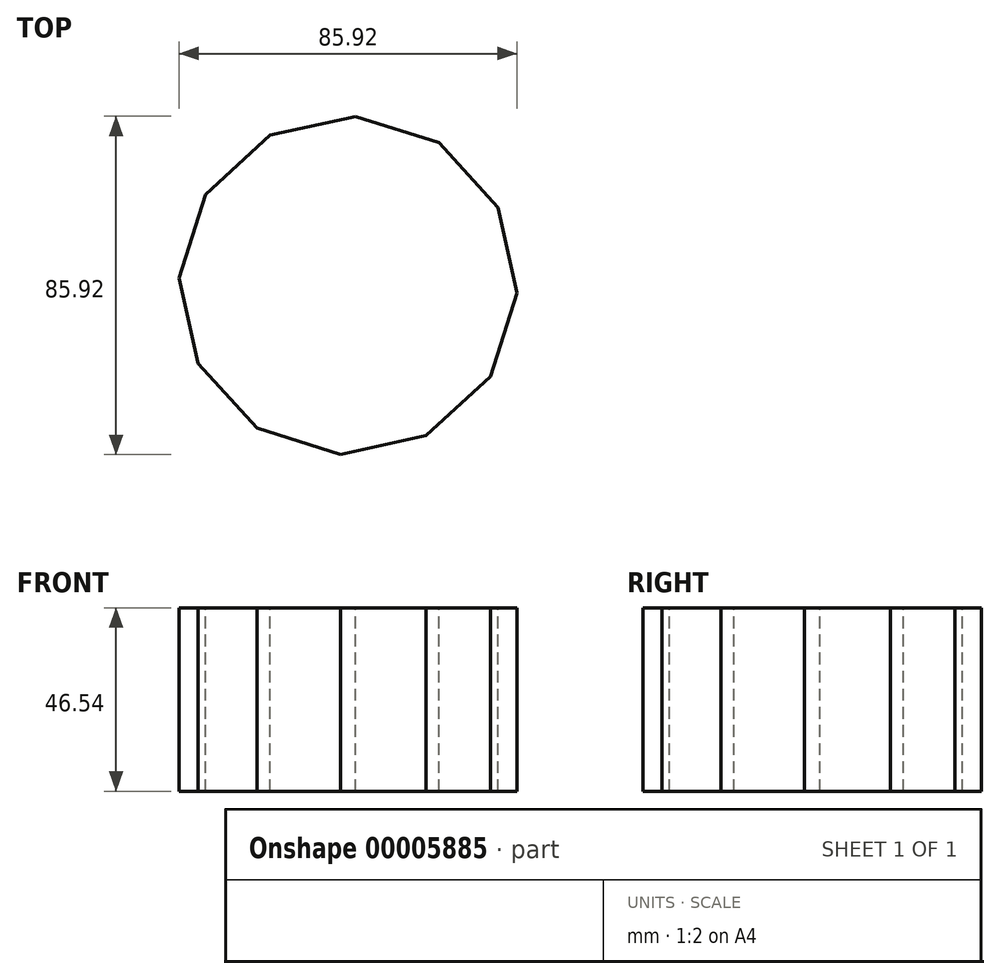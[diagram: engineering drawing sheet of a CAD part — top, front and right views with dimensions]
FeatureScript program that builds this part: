
annotation { "Feature Type Name" : "Feature", "Feature Type Description" : "" }
export const myFeature = defineFeature(function(context is Context, id is Id, definition is map)
    precondition{}
    {
        {
            var Q0;
            Q0=qCreatedBy(makeId("Top.planeOp"),FACE);
            var sketch = newSketch(context, id + "F0", { "sketchPlane" : qUnion([Q0])});
            skCircle(sketch, "E0", {"center": v(15.78, -12.52) * mm, "radius": 79.74 * mm});
            skSolve(sketch);
        }
        {
            var Q0;
            Q0 = qSketchRegion(id + "F0", true);
            extrude(context, id + "F1", {"entities" : qUnion([Q0]), "depth" : 31.75 * mm});
        }
        {
            var Q0;
            Q0=makeQuery(id+"F1.opExtrude","CAP_FACE",FACE,{"disambiguationData":[OSD([sQuery(id+"F0.wireOp",EDGE,"E0")])],"isStart":false});
            var sketch = newSketch(context, id + "F2", { "sketchPlane" : qUnion([Q0])});
            skCircle(sketch, "E1.cCircle", {"center": v(15.78, -12.52) * mm, "radius": 41.53 * mm, "construction": true});
            skLineSegment(sketch, "E1.0", {"start": v(-27.18, -10.61) * mm, "end": v(-20.47, 10.61) * mm});
            skLineSegment(sketch, "E1.1", {"start": v(-20.47, 10.61) * mm, "end": v(-4.05, 25.64) * mm});
            skLineSegment(sketch, "E1.2", {"start": v(-4.05, 25.64) * mm, "end": v(17.69, 30.44) * mm});
            skLineSegment(sketch, "E1.3", {"start": v(17.69, 30.44) * mm, "end": v(38.91, 23.73) * mm});
            skLineSegment(sketch, "E1.4", {"start": v(38.91, 23.73) * mm, "end": v(53.94, 7.3) * mm});
            skLineSegment(sketch, "E1.5", {"start": v(53.94, 7.3) * mm, "end": v(58.74, -14.43) * mm});
            skLineSegment(sketch, "E1.6", {"start": v(58.74, -14.43) * mm, "end": v(52.03, -35.65) * mm});
            skLineSegment(sketch, "E1.7", {"start": v(52.03, -35.65) * mm, "end": v(35.6, -50.68) * mm});
            skLineSegment(sketch, "E1.8", {"start": v(35.6, -50.68) * mm, "end": v(13.87, -55.48) * mm});
            skLineSegment(sketch, "E1.9", {"start": v(13.87, -55.48) * mm, "end": v(-7.35, -48.77) * mm});
            skLineSegment(sketch, "E1.10", {"start": v(-7.35, -48.77) * mm, "end": v(-22.38, -32.35) * mm});
            skLineSegment(sketch, "E1.11", {"start": v(-22.38, -32.35) * mm, "end": v(-27.18, -10.61) * mm});
            skPoint(sketch, "E1.0.midPoint", {"position": v(-23.82, 0) * mm});
            skSolve(sketch);
        }
        {
            var Q0;
            Q0 = qSketchRegion(id + "F2", true);
            extrude(context, id + "F3", {"entities" : qUnion([Q0]), "operationType" : NewBodyOperationType.INTERSECT, "oppositeDirection" : true, "depth" : 95.32 * mm});
        }
        {
            var Q0;
            Q0=makeQuery(id+"F1.opExtrude","CAP_FACE",FACE,{"disambiguationData":[OSD([sQuery(id+"F0.wireOp",EDGE,"E0")])],"isStart":false});
            extrude(context, id + "F4", {"entities" : qUnion([Q0]), "operationType" : NewBodyOperationType.ADD, "depth" : 14.8 * mm});
        }
    });
